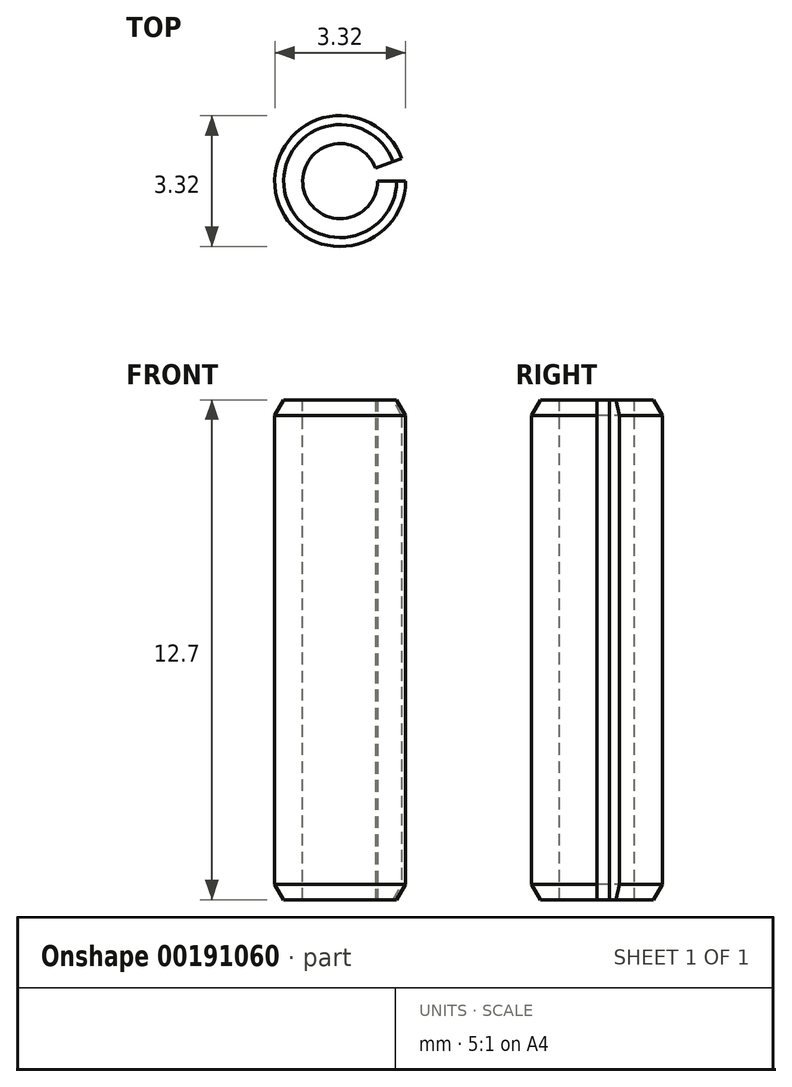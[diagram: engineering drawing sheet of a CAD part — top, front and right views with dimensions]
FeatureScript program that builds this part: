
annotation { "Feature Type Name" : "Feature", "Feature Type Description" : "" }
export const myFeature = defineFeature(function(context is Context, id is Id, definition is map)
    precondition{}
    {
        {
            var Q0;
            Q0=qCreatedBy(makeId("Front.planeOp"),FACE);
            var sketch = newSketch(context, id + "F0", { "sketchPlane" : qUnion([Q0])});
            skLineSegment(sketch, "E0.bottom", {"start": v(0.95, 0) * mm, "end": v(1.66, 0) * mm});
            skLineSegment(sketch, "E0.top", {"start": v(0.95, -12.7) * mm, "end": v(1.66, -12.7) * mm});
            skLineSegment(sketch, "E0.left", {"start": v(0.95, 0) * mm, "end": v(0.95, -12.7) * mm});
            skLineSegment(sketch, "E0.right", {"start": v(1.66, 0) * mm, "end": v(1.66, -12.7) * mm});
            skSolve(sketch);
        }
        {
            var Q0;
            Q0=qCreatedBy(makeId("Front.planeOp"),FACE);
            var sketch = newSketch(context, id + "F1", { "sketchPlane" : qUnion([Q0])});
            skLineSegment(sketch, "E1", {"start": v(0, 0) * mm, "end": v(0, -16.64) * mm, "construction": true});
            skSolve(sketch);
        }
        {
            var Q0;
            Q0=makeQuery(id+"F0.imprint","IMPRINT",FACE,{"disambiguationData":[TD([[makeQuery(id+"F0.imprint","IMPRINT",EDGE,{"derivedFrom":sQuery(id+"F0.wireOp",EDGE,"E0.bottom")}),-1.0]])]});
            var Q1;
            Q1=sQuery(id+"F1.wireOp",EDGE,"E1");
            revolve(context, id + "F2", {"entities" : qUnion([Q0]), "axis" : qUnion([Q1]), "revolveType" : RevolveType.ONE_DIRECTION, "angle" : 340 * degree});
        }
        {
            var Q0;
            Q0=makeQuery(id+"F2.opRevolve","SWEPT_EDGE",EDGE,{"disambiguationData":[OSD([sQuery(id+"F0.wireOp",EDGE,"E0.bottom"),sQuery(id+"F0.wireOp",EDGE,"E0.right")])]});
            var Q1;
            Q1=makeQuery(id+"F2.opRevolve","SWEPT_EDGE",EDGE,{"disambiguationData":[OSD([sQuery(id+"F0.wireOp",EDGE,"E0.top"),sQuery(id+"F0.wireOp",EDGE,"E0.right")])]});
            chamfer(context, id + "F3", {"entities" : qUnion([Q0, Q1]), "chamferType" : ChamferType.OFFSET_ANGLE, "width" : 0.23 * mm, "oppositeDirection" : false, "angle" : 60 * degree, "tangentPropagation" : true});
        }
    });
